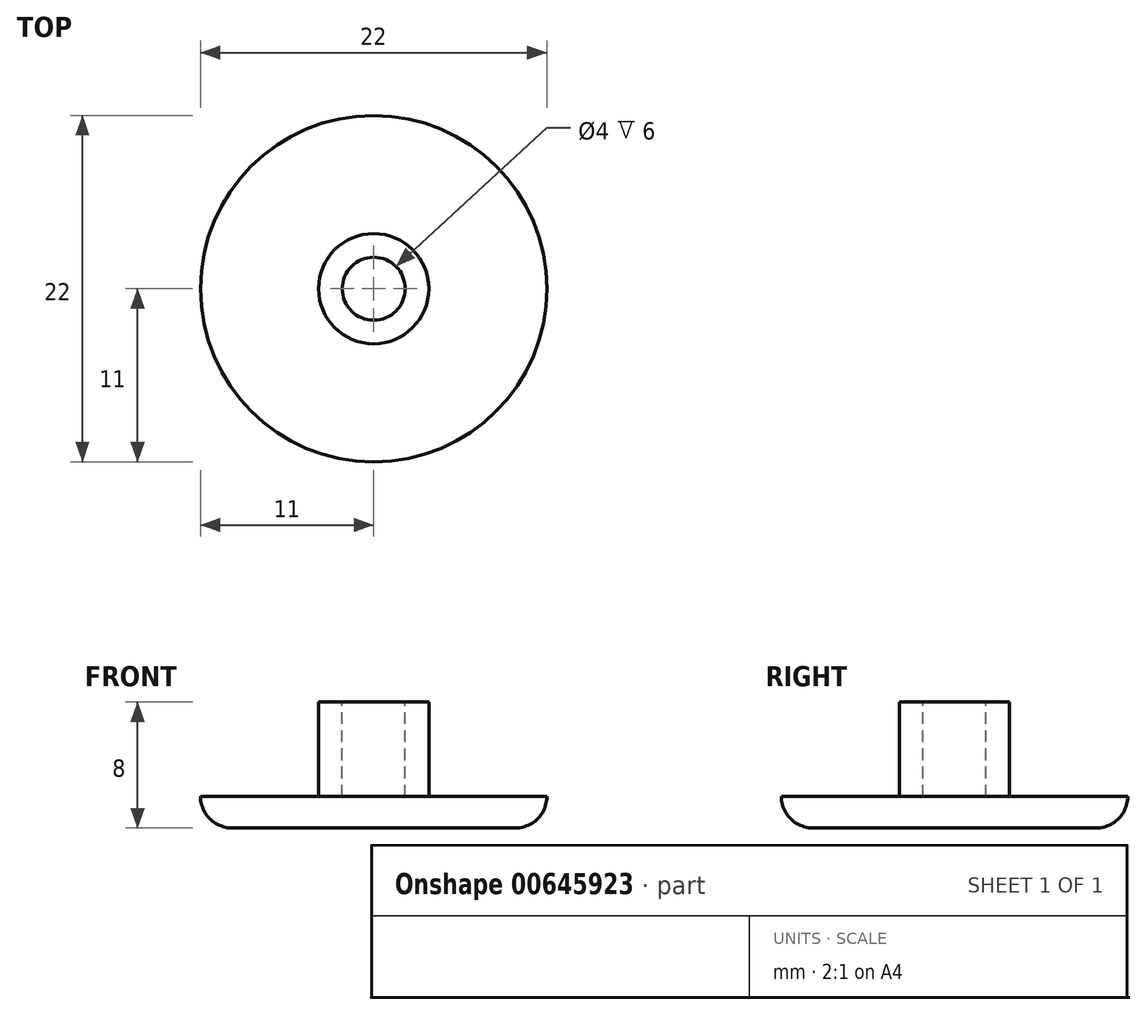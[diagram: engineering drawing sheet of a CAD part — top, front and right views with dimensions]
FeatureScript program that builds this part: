
annotation { "Feature Type Name" : "Feature", "Feature Type Description" : "" }
export const myFeature = defineFeature(function(context is Context, id is Id, definition is map)
    precondition{}
    {
        {
            var Q0;
            Q0=qCreatedBy(makeId("Top.planeOp"),FACE);
            var sketch = newSketch(context, id + "F0", { "sketchPlane" : qUnion([Q0])});
            skCircle(sketch, "E0", {"center": v(0, 0) * mm, "radius": 11 * mm});
            skSolve(sketch);
        }
        {
            var Q0;
            Q0 = qSketchRegion(id + "F0", true);
            extrude(context, id + "F1", {"entities" : qUnion([Q0]), "depth" : 2 * mm, "offsetDistance" : 25 * mm});
        }
        {
            var Q0;
            Q0=makeQuery(id+"F1.opExtrude","CAP_FACE",FACE,{"disambiguationData":[OSD([sQuery(id+"F0.wireOp",EDGE,"E0")])],"isStart":false});
            var sketch = newSketch(context, id + "F2", { "sketchPlane" : qUnion([Q0])});
            skCircle(sketch, "E1", {"center": v(0, 0) * mm, "radius": 3.5 * mm});
            skSolve(sketch);
        }
        {
            var Q0;
            Q0 = qSketchRegion(id + "F2", true);
            extrude(context, id + "F3", {"entities" : qUnion([Q0]), "operationType" : NewBodyOperationType.ADD, "depth" : 6 * mm, "offsetDistance" : 25 * mm});
        }
        {
            var Q0;
            Q0=makeQuery(id+"F3.opExtrude","CAP_FACE",FACE,{"disambiguationData":[OSD([sQuery(id+"F2.wireOp",EDGE,"E1")])],"isStart":false});
            var sketch = newSketch(context, id + "F4", { "sketchPlane" : qUnion([Q0])});
            skCircle(sketch, "E2", {"center": v(0, 0) * mm, "radius": 2 * mm});
            skSolve(sketch);
        }
        {
            var Q0;
            Q0=makeQuery(id+"F4.imprint","IMPRINT",FACE,{"disambiguationData":[TD([[makeQuery(id+"F4.imprint","IMPRINT",EDGE,{"derivedFrom":sQuery(id+"F4.wireOp",EDGE,"E2")}),1.0]])]});
            extrude(context, id + "F5", {"entities" : qUnion([Q0]), "operationType" : NewBodyOperationType.REMOVE, "oppositeDirection" : true, "depth" : 6 * mm, "offsetDistance" : 25 * mm});
        }
        {
            var Q0;
            Q0=makeQuery(id+"F1.opExtrude","CAP_EDGE",EDGE,{"disambiguationData":[OSD([sQuery(id+"F0.wireOp",EDGE,"E0")])],"isStart":true});
            fillet(context, id + "F6", {"entities" : qUnion([Q0]), "radius" : 2 * mm, "tangentPropagation" : true, "allowEdgeOverflow" : false});
        }
    });
